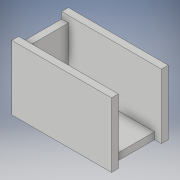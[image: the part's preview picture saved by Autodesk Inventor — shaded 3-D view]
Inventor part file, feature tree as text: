
AUTODESK INVENTOR PART (.ipt)
format: ipt  version: 2019 (Build 230136000, 136)  size: 120,832 bytes
history: native  units: mm
features: extrude x3, sketch x3, projected_geometry x2
ambient origin geometry x8: Origin, YZ Plane, XZ Plane, XY Plane, X Axis, Y Axis, Z Axis, Center Point
bodies: Solid1 (feature_tree)
feature tree (8):
  extrude  "Extrusion1"  Depth=20.0mm
  extrude  "Extrusion2"  Depth=3.18mm
  extrude  "Extrusion3"  Depth=3.18mm
  sketch  "Sketch2"  dims[d25=40.0mm d26=20.0mm]
  sketch  "Sketch5"  dims[d27=3.18mm d28=0.0mm d34=3.18mm]
  projected_geometry  "Projected Loop2"
  sketch  "Sketch6"  dims[d35=3.18mm d36=3.18mm d37=30.0mm d38=0.0mm d39=3.18mm d40=20.0mm d41=27.0mm d42=0.0mm]
  projected_geometry  "Projected Loop3"
